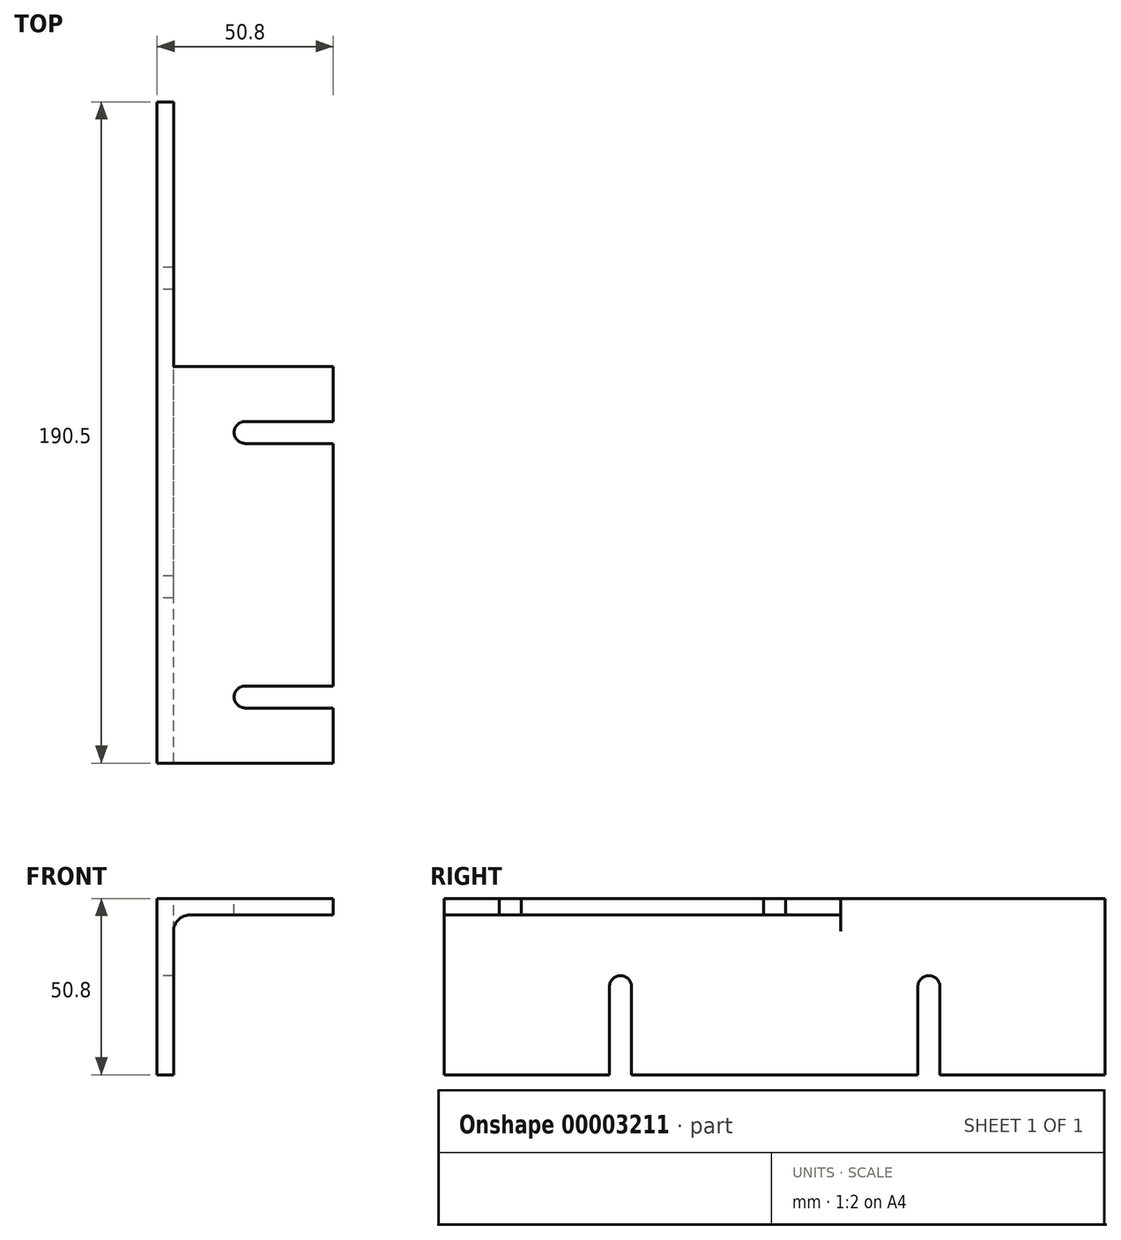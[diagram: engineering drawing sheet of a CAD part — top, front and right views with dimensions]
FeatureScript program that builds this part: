
annotation { "Feature Type Name" : "Feature", "Feature Type Description" : "" }
export const myFeature = defineFeature(function(context is Context, id is Id, definition is map)
    precondition{}
    {
        {
            var Q0;
            Q0=qCreatedBy(makeId("Front.planeOp"),FACE);
            var sketch = newSketch(context, id + "F0", { "sketchPlane" : qUnion([Q0])});
            skLineSegment(sketch, "E0", {"start": v(0, 0) * mm, "end": v(0, -50.8) * mm});
            skLineSegment(sketch, "E1", {"start": v(0, -50.8) * mm, "end": v(4.75, -50.8) * mm});
            skLineSegment(sketch, "E2", {"start": v(4.75, -50.8) * mm, "end": v(4.75, -9.5) * mm});
            skLineSegment(sketch, "E3", {"start": v(9.5, -4.75) * mm, "end": v(50.8, -4.75) * mm});
            skLineSegment(sketch, "E4", {"start": v(50.8, -4.75) * mm, "end": v(50.8, 0) * mm});
            skLineSegment(sketch, "E5", {"start": v(50.8, 0) * mm, "end": v(0, 0) * mm});
            skArc(sketch, "E6", {"start": v(9.5, -4.75) * mm, "mid": v(6.14, -6.14) * mm, "end": v(4.75, -9.5) * mm});
            skSolve(sketch);
        }
        {
            var Q0;
            Q0=makeQuery(id+"F0.imprint","IMPRINT",FACE,{"disambiguationData":[TD([[makeQuery(id+"F0.imprint","IMPRINT",EDGE,{"derivedFrom":sQuery(id+"F0.wireOp",EDGE,"E0")}),1.0]])]});
            extrude(context, id + "F1", {"entities" : qUnion([Q0]), "endBound" : BoundingType.SYMMETRIC, "depth" : 190.5 * mm});
        }
        {
            var Q0;
            Q0=makeQuery(id+"F1.opExtrude","SWEPT_FACE",FACE,{"disambiguationData":[OSD([sQuery(id+"F0.wireOp",EDGE,"E5")])]});
            var sketch = newSketch(context, id + "F2", { "sketchPlane" : qUnion([Q0])});
            skLineSegment(sketch, "E7", {"start": v(25.4, 95.25) * mm, "end": v(25.4, -95.25) * mm, "construction": true});
            skLineSegment(sketch, "E8", {"start": v(0, 0) * mm, "end": v(50.8, 0) * mm, "construction": true});
            skLineSegment(sketch, "E9", {"start": v(0, -76.2) * mm, "end": v(50.8, -76.2) * mm, "construction": true});
            skCircle(sketch, "E10", {"center": v(25.4, 0) * mm, "radius": 3.18 * mm});
            skCircle(sketch, "E11", {"center": v(25.4, -76.2) * mm, "radius": 3.18 * mm});
            skLineSegment(sketch, "E12", {"start": v(50.8, 19.05) * mm, "end": v(4.75, 19.05) * mm});
            skLineSegment(sketch, "E13", {"start": v(4.75, 95.25) * mm, "end": v(4.75, 19.05) * mm});
            skPoint(sketch, "E14.orphan", {"position": v(0, 19.05) * mm});
            skLineSegment(sketch, "E15", {"start": v(25.4, 3.17) * mm, "end": v(50.8, 3.17) * mm});
            skLineSegment(sketch, "E16", {"start": v(25.4, -3.18) * mm, "end": v(50.8, -3.18) * mm});
            skLineSegment(sketch, "E17", {"start": v(25.4, -73.03) * mm, "end": v(50.8, -73.03) * mm});
            skLineSegment(sketch, "E18", {"start": v(25.4, -79.38) * mm, "end": v(50.8, -79.38) * mm});
            skSolve(sketch);
        }
        {
            var Q0;
            {var subQ5=sQuery(id+"F2.wireOp",EDGE,"E12");Q0=makeQuery(id+"F2.imprint","IMPRINT",FACE,{"disambiguationData":[TD([[makeQuery(id+"F2.imprint","IMPRINT",EDGE,{"derivedFrom":subQ5}),-1.0]])]});}
            extrude(context, id + "F3", {"entities" : qUnion([Q0]), "operationType" : NewBodyOperationType.REMOVE, "endBound" : BoundingType.THROUGH_ALL, "oppositeDirection" : true, "depth" : 25.4 * mm});
        }
        {
            var Q0;
            Q0 = qSketchRegion(id + "F2", true);
            extrude(context, id + "F4", {"entities" : qUnion([Q0]), "operationType" : NewBodyOperationType.REMOVE, "oppositeDirection" : true, "depth" : 25.4 * mm});
        }
        {
            var Q0;
            {var subQ2=sQuery(id+"F2.wireOp",EDGE,"E15");Q0=makeQuery(id+"F2.imprint","IMPRINT",FACE,{"disambiguationData":[TD([[makeQuery(id+"F2.imprint","IMPRINT",EDGE,{"derivedFrom":subQ2}),-1.0]])]});}
            var Q1;
            {var subQ2=sQuery(id+"F2.wireOp",EDGE,"E17");Q1=makeQuery(id+"F2.imprint","IMPRINT",FACE,{"disambiguationData":[TD([[makeQuery(id+"F2.imprint","IMPRINT",EDGE,{"derivedFrom":subQ2}),-1.0]])]});}
            extrude(context, id + "F5", {"entities" : qUnion([Q0, Q1]), "operationType" : NewBodyOperationType.REMOVE, "endBound" : BoundingType.THROUGH_ALL, "oppositeDirection" : true, "depth" : 25.4 * mm});
        }
        {
            var Q0;
            Q0=makeQuery(id+"F1.opExtrude","SWEPT_FACE",FACE,{"disambiguationData":[OSD([sQuery(id+"F0.wireOp",EDGE,"E0")])]});
            var sketch = newSketch(context, id + "F6", { "sketchPlane" : qUnion([Q0])});
            skLineSegment(sketch, "E19", {"start": v(-95.25, -25.4) * mm, "end": v(92.62, -25.4) * mm, "construction": true});
            skLineSegment(sketch, "E20", {"start": v(-44.45, -50.8) * mm, "end": v(-44.45, 0) * mm, "construction": true});
            skLineSegment(sketch, "E21", {"start": v(44.45, -50.8) * mm, "end": v(44.45, 0) * mm, "construction": true});
            skCircle(sketch, "E22", {"center": v(-44.45, -25.4) * mm, "radius": 3.18 * mm});
            skCircle(sketch, "E23", {"center": v(44.45, -25.4) * mm, "radius": 3.18 * mm});
            skLineSegment(sketch, "E24", {"start": v(-47.63, -25.4) * mm, "end": v(-47.63, -50.8) * mm});
            skLineSegment(sketch, "E25", {"start": v(-41.28, -25.4) * mm, "end": v(-41.28, -50.8) * mm});
            skLineSegment(sketch, "E26", {"start": v(41.28, -25.4) * mm, "end": v(41.28, -50.8) * mm});
            skLineSegment(sketch, "E27", {"start": v(47.62, -25.4) * mm, "end": v(47.62, -50.8) * mm});
            skSolve(sketch);
        }
        {
            var Q0;
            Q0 = qSketchRegion(id + "F6", true);
            var Q1;
            {var subQ2=sQuery(id+"F6.wireOp",EDGE,"E24");Q1=makeQuery(id+"F6.imprint","IMPRINT",FACE,{"disambiguationData":[TD([[makeQuery(id+"F6.imprint","IMPRINT",EDGE,{"derivedFrom":subQ2}),1.0]])]});}
            var Q2;
            {var subQ2=sQuery(id+"F6.wireOp",EDGE,"E26");Q2=makeQuery(id+"F6.imprint","IMPRINT",FACE,{"disambiguationData":[TD([[makeQuery(id+"F6.imprint","IMPRINT",EDGE,{"derivedFrom":subQ2}),1.0]])]});}
            extrude(context, id + "F7", {"entities" : qUnion([Q0, Q1, Q2]), "operationType" : NewBodyOperationType.REMOVE, "endBound" : BoundingType.THROUGH_ALL, "oppositeDirection" : true, "depth" : 25.4 * mm});
        }
    });
